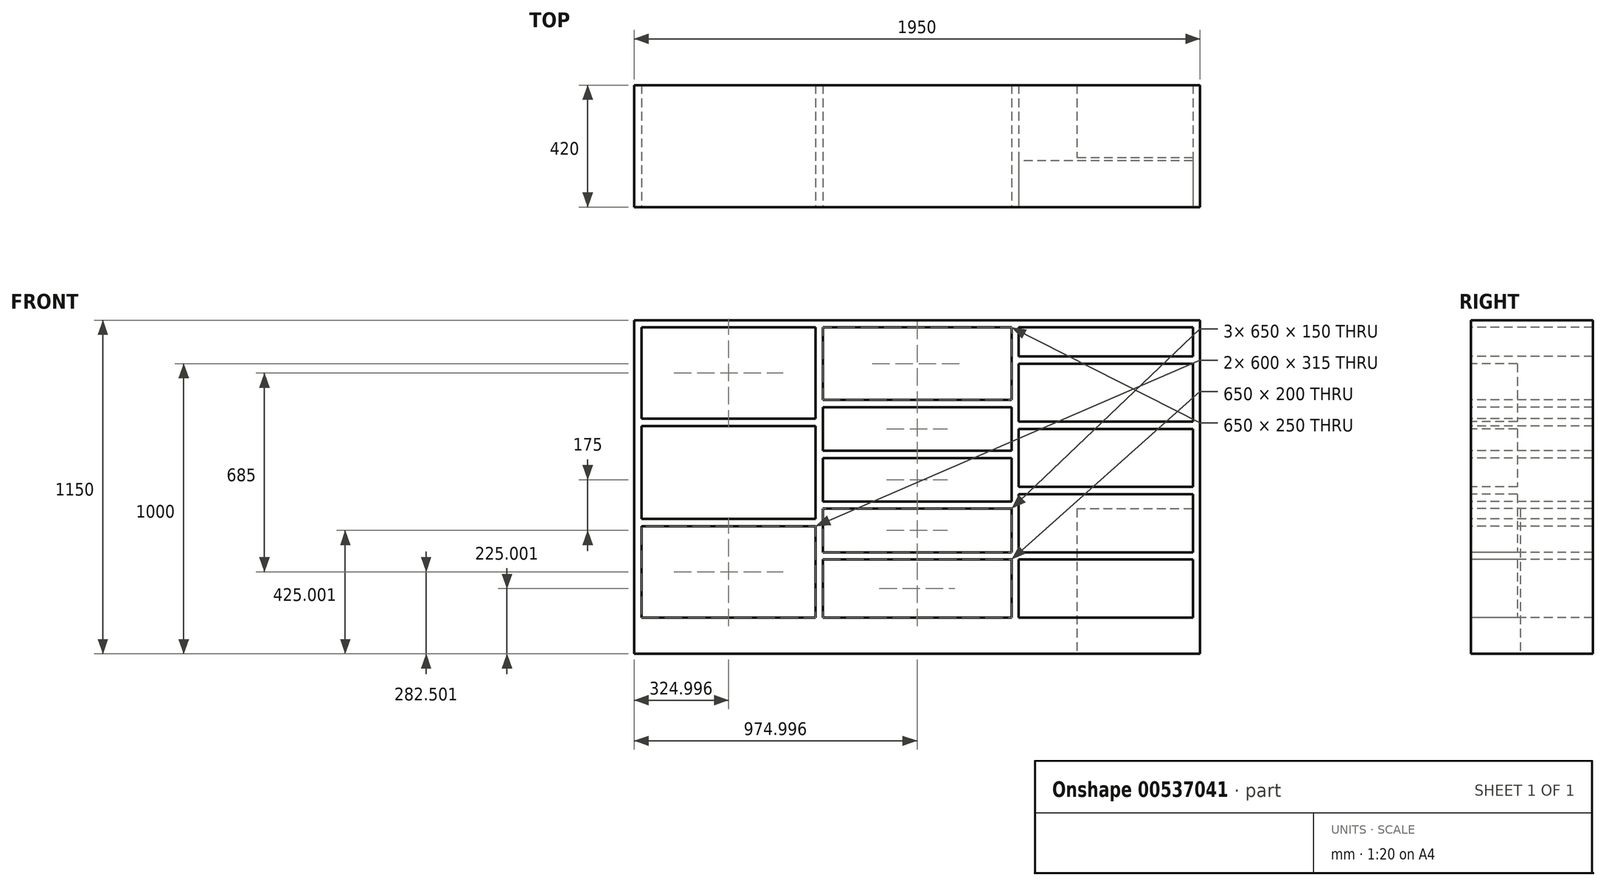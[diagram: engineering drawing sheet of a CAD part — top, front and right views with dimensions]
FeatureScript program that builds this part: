
annotation { "Feature Type Name" : "Feature", "Feature Type Description" : "" }
export const myFeature = defineFeature(function(context is Context, id is Id, definition is map)
    precondition{}
    {
        {
            var Q0;
            Q0=qCreatedBy(makeId("Front.planeOp"),FACE);
            var sketch = newSketch(context, id + "F0", { "sketchPlane" : qUnion([Q0])});
            skLineSegment(sketch, "E0.bottom", {"start": v(-40.3, 1117.31) * mm, "end": v(1909.7, 1117.31) * mm});
            skLineSegment(sketch, "E0.top", {"start": v(-40.3, -32.69) * mm, "end": v(1909.7, -32.69) * mm});
            skLineSegment(sketch, "E0.left", {"start": v(-40.3, 1117.31) * mm, "end": v(-40.3, -32.69) * mm});
            skLineSegment(sketch, "E0.right", {"start": v(1909.7, 1117.31) * mm, "end": v(1909.7, -32.69) * mm});
            skSolve(sketch);
        }
        {
            var Q0;
            Q0=makeQuery(id+"F0.imprint","IMPRINT",FACE,{"disambiguationData":[TD([[makeQuery(id+"F0.imprint","IMPRINT",EDGE,{"derivedFrom":sQuery(id+"F0.wireOp",EDGE,"E0.bottom")}),-1.0]])]});
            extrude(context, id + "F1", {"entities" : qUnion([Q0]), "depth" : 420 * mm, "offsetDistance" : 25 * mm});
        }
        {
            var Q0;
            Q0=makeQuery(id+"F1.opExtrude","CAP_FACE",FACE,{"disambiguationData":[OSD([sQuery(id+"F0.wireOp",EDGE,"E0.bottom"),sQuery(id+"F0.wireOp",EDGE,"E0.top"),sQuery(id+"F0.wireOp",EDGE,"E0.left"),sQuery(id+"F0.wireOp",EDGE,"E0.right")])],"isStart":false});
            var sketch = newSketch(context, id + "F2", { "sketchPlane" : qUnion([Q0])});
            skLineSegment(sketch, "E1.bottom", {"start": v(-15.3, 1092.31) * mm, "end": v(584.7, 1092.31) * mm});
            skLineSegment(sketch, "E1.top", {"start": v(-15.3, 92.31) * mm, "end": v(584.7, 92.31) * mm});
            skLineSegment(sketch, "E1.left", {"start": v(-15.3, 1092.31) * mm, "end": v(-15.3, 92.31) * mm});
            skLineSegment(sketch, "E1.right", {"start": v(584.7, 1092.31) * mm, "end": v(584.7, 92.31) * mm});
            skLineSegment(sketch, "E2.bottom", {"start": v(609.7, 1092.31) * mm, "end": v(1259.7, 1092.31) * mm});
            skLineSegment(sketch, "E2.top", {"start": v(609.7, 92.31) * mm, "end": v(1259.7, 92.31) * mm});
            skLineSegment(sketch, "E2.left", {"start": v(609.7, 1092.31) * mm, "end": v(609.7, 92.31) * mm});
            skLineSegment(sketch, "E2.right", {"start": v(1259.7, 1092.31) * mm, "end": v(1259.7, 92.31) * mm});
            skLineSegment(sketch, "E3.bottom", {"start": v(1284.7, 1092.31) * mm, "end": v(1884.7, 1092.31) * mm});
            skLineSegment(sketch, "E3.top", {"start": v(1284.7, 92.31) * mm, "end": v(1884.7, 92.31) * mm});
            skLineSegment(sketch, "E3.left", {"start": v(1284.7, 1092.31) * mm, "end": v(1284.7, 92.31) * mm});
            skLineSegment(sketch, "E3.right", {"start": v(1884.7, 1092.31) * mm, "end": v(1884.7, 92.31) * mm});
            skLineSegment(sketch, "E4", {"start": v(609.7, 842.31) * mm, "end": v(1259.7, 842.31) * mm});
            skLineSegment(sketch, "E5", {"start": v(609.7, 817.31) * mm, "end": v(1259.7, 817.31) * mm});
            skLineSegment(sketch, "E6", {"start": v(609.7, 667.31) * mm, "end": v(1259.7, 667.31) * mm});
            skLineSegment(sketch, "E7", {"start": v(609.7, 642.31) * mm, "end": v(1259.7, 642.31) * mm});
            skLineSegment(sketch, "E8", {"start": v(609.7, 492.31) * mm, "end": v(1259.7, 492.31) * mm});
            skLineSegment(sketch, "E9", {"start": v(609.7, 467.31) * mm, "end": v(1259.7, 467.31) * mm});
            skLineSegment(sketch, "E10", {"start": v(609.7, 317.31) * mm, "end": v(1259.7, 317.31) * mm});
            skLineSegment(sketch, "E11", {"start": v(609.7, 292.31) * mm, "end": v(1259.7, 292.31) * mm});
            skLineSegment(sketch, "E12", {"start": v(1884.7, 872.31) * mm, "end": v(1884.7, 847.31) * mm});
            skLineSegment(sketch, "E13", {"start": v(1284.7, 847.31) * mm, "end": v(1284.7, 627.31) * mm});
            skLineSegment(sketch, "E14", {"start": v(1884.7, 627.31) * mm, "end": v(1884.7, 602.31) * mm});
            skLineSegment(sketch, "E15", {"start": v(1284.7, 602.31) * mm, "end": v(1284.7, 382.31) * mm});
            skLineSegment(sketch, "E16", {"start": v(1884.7, 382.31) * mm, "end": v(1884.7, 357.31) * mm});
            skLineSegment(sketch, "E17", {"start": v(1284.7, 357.31) * mm, "end": v(1284.7, 137.31) * mm});
            skLineSegment(sketch, "E18", {"start": v(1884.7, 137.31) * mm, "end": v(1884.7, 112.31) * mm});
            skLineSegment(sketch, "E19", {"start": v(-15.3, 777.31) * mm, "end": v(584.7, 777.31) * mm});
            skLineSegment(sketch, "E20", {"start": v(584.7, 777.31) * mm, "end": v(584.7, 752.31) * mm});
            skLineSegment(sketch, "E21", {"start": v(584.7, 752.31) * mm, "end": v(-15.3, 752.31) * mm});
            skLineSegment(sketch, "E22", {"start": v(-15.3, 752.31) * mm, "end": v(-15.3, 432.31) * mm});
            skLineSegment(sketch, "E23", {"start": v(-15.3, 432.31) * mm, "end": v(584.7, 432.31) * mm});
            skLineSegment(sketch, "E24", {"start": v(584.7, 432.31) * mm, "end": v(584.7, 407.31) * mm});
            skLineSegment(sketch, "E25", {"start": v(584.7, 407.31) * mm, "end": v(-15.3, 407.31) * mm});
            skSolve(sketch);
        }
        {
            var Q0;
            {var subQ0=sQuery(id+"F2.wireOp",EDGE,"E2.top");Q0=makeQuery(id+"F2.imprint","IMPRINT",FACE,{"disambiguationData":[TD([[makeQuery(id+"F2.imprint","IMPRINT",EDGE,{"derivedFrom":subQ0}),1.0]])]});}
            var Q1;
            {var subQ0=sQuery(id+"F2.wireOp",EDGE,"E9");Q1=makeQuery(id+"F2.imprint","IMPRINT",FACE,{"disambiguationData":[TD([[makeQuery(id+"F2.imprint","IMPRINT",EDGE,{"derivedFrom":subQ0}),-1.0]])]});}
            var Q2;
            {var subQ0=sQuery(id+"F2.wireOp",EDGE,"E7");Q2=makeQuery(id+"F2.imprint","IMPRINT",FACE,{"disambiguationData":[TD([[makeQuery(id+"F2.imprint","IMPRINT",EDGE,{"derivedFrom":subQ0}),-1.0]])]});}
            var Q3;
            {var subQ0=sQuery(id+"F2.wireOp",EDGE,"E5");Q3=makeQuery(id+"F2.imprint","IMPRINT",FACE,{"disambiguationData":[TD([[makeQuery(id+"F2.imprint","IMPRINT",EDGE,{"derivedFrom":subQ0}),-1.0]])]});}
            var Q4;
            {var subQ0=sQuery(id+"F2.wireOp",EDGE,"E2.bottom");Q4=makeQuery(id+"F2.imprint","IMPRINT",FACE,{"disambiguationData":[TD([[makeQuery(id+"F2.imprint","IMPRINT",EDGE,{"derivedFrom":subQ0}),-1.0]])]});}
            var Q5;
            {var subQ0=sQuery(id+"F2.wireOp",EDGE,"E1.bottom");Q5=makeQuery(id+"F2.imprint","IMPRINT",FACE,{"disambiguationData":[TD([[makeQuery(id+"F2.imprint","IMPRINT",EDGE,{"derivedFrom":subQ0}),-1.0]])]});}
            var Q6;
            {var subQ0=sQuery(id+"F2.wireOp",EDGE,"E21");Q6=makeQuery(id+"F2.imprint","IMPRINT",FACE,{"disambiguationData":[TD([[makeQuery(id+"F2.imprint","IMPRINT",EDGE,{"derivedFrom":subQ0}),1.0]])]});}
            var Q7;
            {var subQ0=sQuery(id+"F2.wireOp",EDGE,"E1.top");Q7=makeQuery(id+"F2.imprint","IMPRINT",FACE,{"disambiguationData":[TD([[makeQuery(id+"F2.imprint","IMPRINT",EDGE,{"derivedFrom":subQ0}),1.0]])]});}
            extrude(context, id + "F3", {"entities" : qUnion([Q0, Q1, Q2, Q3, Q4, Q5, Q6, Q7]), "operationType" : NewBodyOperationType.REMOVE, "oppositeDirection" : true, "depth" : 450 * mm, "offsetDistance" : 25 * mm});
        }
        {
            var Q0;
            Q0=makeQuery(id+"F1.opExtrude","CAP_FACE",FACE,{"disambiguationData":[OSD([sQuery(id+"F0.wireOp",EDGE,"E0.bottom"),sQuery(id+"F0.wireOp",EDGE,"E0.top"),sQuery(id+"F0.wireOp",EDGE,"E0.left"),sQuery(id+"F0.wireOp",EDGE,"E0.right")])],"isStart":false});
            var sketch = newSketch(context, id + "F4", { "sketchPlane" : qUnion([Q0])});
            skLineSegment(sketch, "E26.bottom", {"start": v(1284.7, 1092.31) * mm, "end": v(1884.7, 1092.31) * mm});
            skLineSegment(sketch, "E26.top", {"start": v(1284.7, 92.31) * mm, "end": v(1884.7, 92.31) * mm});
            skLineSegment(sketch, "E26.left", {"start": v(1284.7, 1092.31) * mm, "end": v(1284.7, 92.31) * mm});
            skLineSegment(sketch, "E26.right", {"start": v(1884.7, 1092.31) * mm, "end": v(1884.7, 92.31) * mm});
            skLineSegment(sketch, "E27", {"start": v(1284.7, 767.31) * mm, "end": v(1884.7, 767.31) * mm});
            skLineSegment(sketch, "E28", {"start": v(1884.7, 767.31) * mm, "end": v(1884.7, 742.31) * mm});
            skLineSegment(sketch, "E29", {"start": v(1884.7, 742.31) * mm, "end": v(1284.7, 742.31) * mm});
            skLineSegment(sketch, "E30", {"start": v(1284.7, 842.31) * mm, "end": v(1284.7, 742.31) * mm});
            skLineSegment(sketch, "E31", {"start": v(1884.7, 842.31) * mm, "end": v(1884.7, 817.31) * mm});
            skLineSegment(sketch, "E32", {"start": v(1284.7, 817.31) * mm, "end": v(1284.7, 542.31) * mm});
            skLineSegment(sketch, "E33", {"start": v(1284.7, 542.31) * mm, "end": v(1884.7, 542.31) * mm});
            skLineSegment(sketch, "E34", {"start": v(1884.7, 542.31) * mm, "end": v(1884.7, 517.31) * mm});
            skLineSegment(sketch, "E35", {"start": v(1884.7, 517.31) * mm, "end": v(1284.7, 517.31) * mm});
            skLineSegment(sketch, "E36", {"start": v(1284.7, 317.31) * mm, "end": v(1884.7, 317.31) * mm});
            skLineSegment(sketch, "E37", {"start": v(1884.7, 317.31) * mm, "end": v(1884.7, 292.31) * mm});
            skLineSegment(sketch, "E38", {"start": v(1884.7, 292.31) * mm, "end": v(1284.7, 292.31) * mm});
            skLineSegment(sketch, "E39", {"start": v(1284.7, 967.31) * mm, "end": v(1884.7, 967.31) * mm});
            skLineSegment(sketch, "E40", {"start": v(1284.7, 992.31) * mm, "end": v(1884.7, 992.31) * mm});
            skSolve(sketch);
        }
        {
            var Q0;
            {var subQ0=sQuery(id+"F4.wireOp",EDGE,"E27");Q0=makeQuery(id+"F4.imprint","IMPRINT",FACE,{"disambiguationData":[TD([[makeQuery(id+"F4.imprint","IMPRINT",EDGE,{"derivedFrom":subQ0}),1.0]])]});}
            var Q1;
            {var subQ0=sQuery(id+"F4.wireOp",EDGE,"E29");Q1=makeQuery(id+"F4.imprint","IMPRINT",FACE,{"disambiguationData":[TD([[makeQuery(id+"F4.imprint","IMPRINT",EDGE,{"derivedFrom":subQ0}),1.0]])]});}
            var Q2;
            {var subQ0=sQuery(id+"F4.wireOp",EDGE,"E35");Q2=makeQuery(id+"F4.imprint","IMPRINT",FACE,{"disambiguationData":[TD([[makeQuery(id+"F4.imprint","IMPRINT",EDGE,{"derivedFrom":subQ0}),1.0]])]});}
            var Q3;
            {var subQ0=sQuery(id+"F4.wireOp",EDGE,"E26.top");Q3=makeQuery(id+"F4.imprint","IMPRINT",FACE,{"disambiguationData":[TD([[makeQuery(id+"F4.imprint","IMPRINT",EDGE,{"derivedFrom":subQ0}),1.0]])]});}
            extrude(context, id + "F5", {"entities" : qUnion([Q0, Q1, Q2, Q3]), "operationType" : NewBodyOperationType.REMOVE, "oppositeDirection" : true, "depth" : 160 * mm, "offsetDistance" : 25 * mm});
        }
        {
            var Q0;
            Q0=makeQuery(id+"F1.opExtrude","CAP_FACE",FACE,{"disambiguationData":[OSD([sQuery(id+"F0.wireOp",EDGE,"E0.bottom"),sQuery(id+"F0.wireOp",EDGE,"E0.top"),sQuery(id+"F0.wireOp",EDGE,"E0.left"),sQuery(id+"F0.wireOp",EDGE,"E0.right")])],"isStart":false});
            var sketch = newSketch(context, id + "F6", { "sketchPlane" : qUnion([Q0])});
            skLineSegment(sketch, "E41.bottom", {"start": v(1284.7, 1092.31) * mm, "end": v(1884.7, 1092.31) * mm});
            skLineSegment(sketch, "E41.top", {"start": v(1284.7, 992.31) * mm, "end": v(1884.7, 992.31) * mm});
            skLineSegment(sketch, "E41.left", {"start": v(1284.7, 1092.31) * mm, "end": v(1284.7, 992.31) * mm});
            skLineSegment(sketch, "E41.right", {"start": v(1884.7, 1092.31) * mm, "end": v(1884.7, 992.31) * mm});
            skSolve(sketch);
        }
        {
            var Q0;
            Q0=makeQuery(id+"F6.imprint","IMPRINT",FACE,{"disambiguationData":[TD([[makeQuery(id+"F6.imprint","IMPRINT",EDGE,{"derivedFrom":sQuery(id+"F6.wireOp",EDGE,"E41.bottom")}),-1.0]])]});
            extrude(context, id + "F7", {"entities" : qUnion([Q0]), "operationType" : NewBodyOperationType.REMOVE, "oppositeDirection" : true, "depth" : 450 * mm, "offsetDistance" : 25 * mm});
        }
        {
            var Q0;
            Q0=makeQuery(id+"F1.opExtrude","SWEPT_FACE",FACE,{"disambiguationData":[OSD([sQuery(id+"F0.wireOp",EDGE,"E0.top")])]});
            var sketch = newSketch(context, id + "F8", { "sketchPlane" : qUnion([Q0])});
            skLineSegment(sketch, "E42.bottom", {"start": v(1884.7, 0) * mm, "end": v(1484.7, 0) * mm});
            skLineSegment(sketch, "E42.top", {"start": v(1884.7, 250) * mm, "end": v(1484.7, 250) * mm});
            skLineSegment(sketch, "E42.left", {"start": v(1884.7, 0) * mm, "end": v(1884.7, 250) * mm});
            skLineSegment(sketch, "E42.right", {"start": v(1484.7, 0) * mm, "end": v(1484.7, 250) * mm});
            skSolve(sketch);
        }
        {
            var Q0;
            Q0=makeQuery(id+"F8.imprint","IMPRINT",FACE,{"disambiguationData":[TD([[makeQuery(id+"F8.imprint","IMPRINT",EDGE,{"derivedFrom":sQuery(id+"F8.wireOp",EDGE,"E42.bottom")}),1.0]])]});
            extrude(context, id + "F9", {"entities" : qUnion([Q0]), "operationType" : NewBodyOperationType.REMOVE, "oppositeDirection" : true, "depth" : 500 * mm, "offsetDistance" : 25 * mm});
        }
    });
